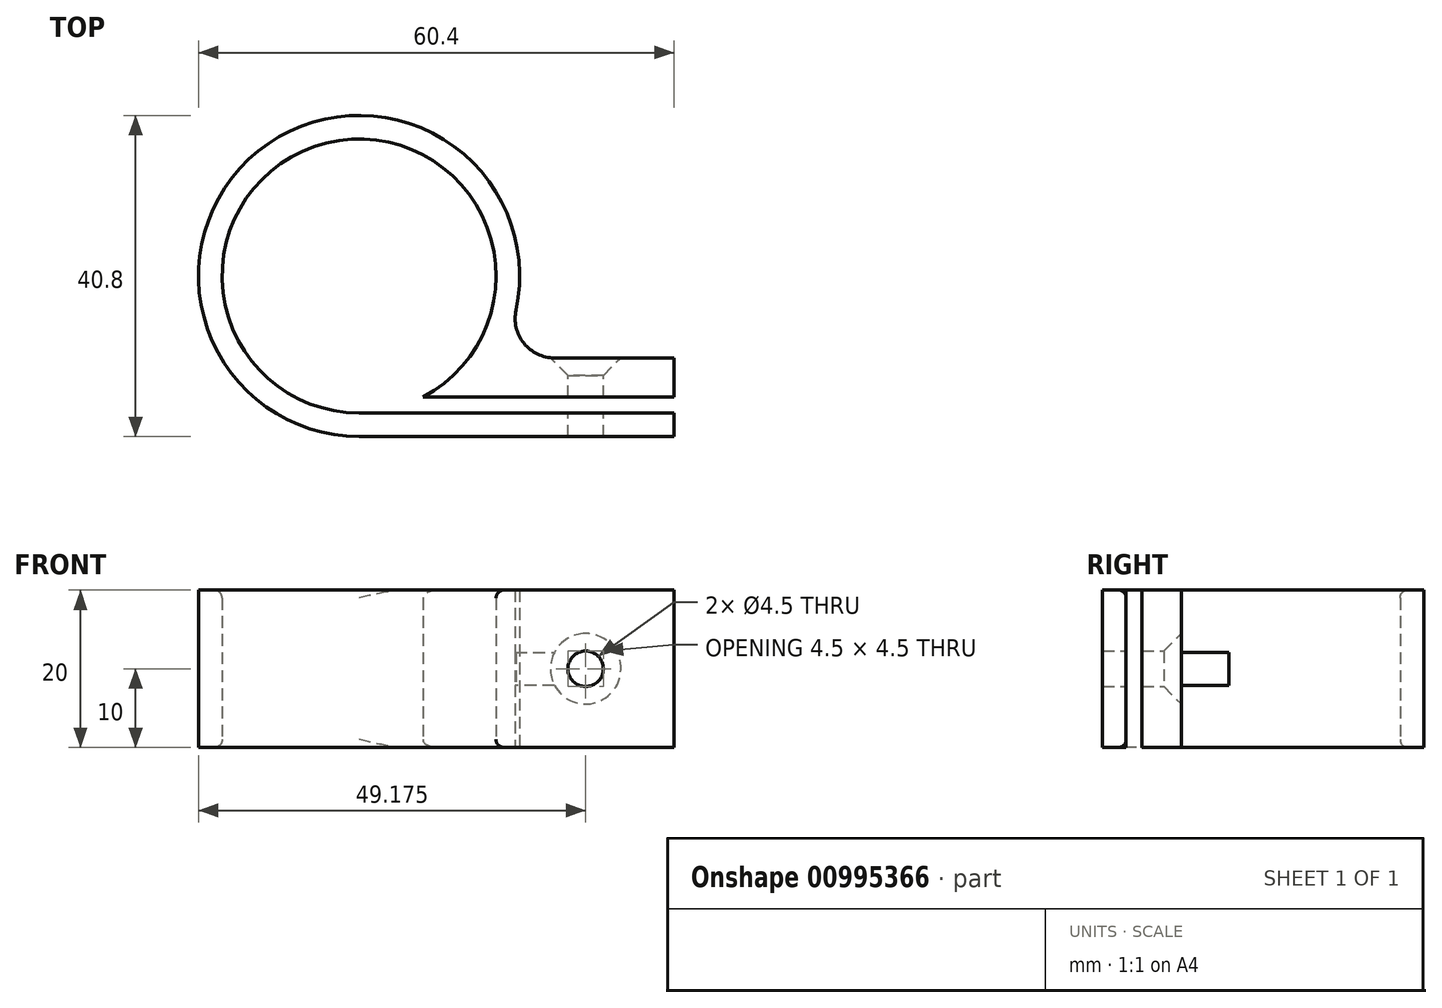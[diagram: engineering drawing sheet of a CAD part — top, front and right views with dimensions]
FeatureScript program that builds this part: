
annotation { "Feature Type Name" : "Feature", "Feature Type Description" : "" }
export const myFeature = defineFeature(function(context is Context, id is Id, definition is map)
    precondition{}
    {
        {
            var Q0;
            Q0=qCreatedBy(makeId("Top.planeOp"),FACE);
            var sketch = newSketch(context, id + "F0", { "sketchPlane" : qUnion([Q0])});
            skCircle(sketch, "E0", {"center": v(0, 0) * mm, "radius": 17.4 * mm});
            skCircle(sketch, "E1.0", {"center": v(0, 0) * mm, "radius": 20.4 * mm});
            skLineSegment(sketch, "E2", {"start": v(0, -20.4) * mm, "end": v(40, -20.4) * mm});
            skLineSegment(sketch, "E3", {"start": v(40, -20.4) * mm, "end": v(40, -10.4) * mm});
            skLineSegment(sketch, "E4", {"start": v(40, -10.4) * mm, "end": v(17.55, -10.4) * mm});
            skLineSegment(sketch, "E5", {"start": v(40, -15.4) * mm, "end": v(8.1, -15.4) * mm});
            skLineSegment(sketch, "E6", {"start": v(40, -17.4) * mm, "end": v(-5.83, -17.4) * mm});
            skSolve(sketch);
        }
        {
            var Q0;
            {var subQ3=sQuery(id+"F0.wireOp",EDGE,"E5");var subQ7=sQuery(id+"F0.wireOp",EDGE,"E0");var subQ8=makeQuery(id+"F0.imprint","INTERSECT",VERTEX,{"derivedFrom":[subQ7,subQ3]});Q0=makeQuery(id+"F0.imprint","IMPRINT",FACE,{"disambiguationData":[TD([[makeQuery(id+"F0.imprint","IMPRINT",EDGE,{"disambiguationData":[TD([[subQ8,-1.0]])],"derivedFrom":subQ7}),-1.0]])]});}
            var Q1;
            {var subQ0=sQuery(id+"F0.wireOp",EDGE,"E2");Q1=makeQuery(id+"F0.imprint","IMPRINT",FACE,{"disambiguationData":[TD([[makeQuery(id+"F0.imprint","IMPRINT",EDGE,{"derivedFrom":subQ0}),1.0]])]});}
            var Q2;
            {var subQ0=sQuery(id+"F0.wireOp",EDGE,"E4");Q2=makeQuery(id+"F0.imprint","IMPRINT",FACE,{"disambiguationData":[TD([[makeQuery(id+"F0.imprint","IMPRINT",EDGE,{"derivedFrom":subQ0}),1.0]])]});}
            extrude(context, id + "F1", {"entities" : qUnion([Q0, Q1, Q2]), "depth" : 20 * mm, "offsetDistance" : 25 * mm});
        }
        {
            var Q0;
            Q0=makeQuery(id+"F1.opExtrude","SWEPT_FACE",FACE,{"disambiguationData":[OSD([sQuery(id+"F0.wireOp",EDGE,"E4")])]});
            var sketch = newSketch(context, id + "F2", { "sketchPlane" : qUnion([Q0])});
            skLineSegment(sketch, "E7.0.0", {"start": v(-40, 0) * mm, "end": v(-17.55, 0) * mm});
            skLineSegment(sketch, "E7.0.1", {"start": v(-17.55, 0) * mm, "end": v(-17.55, 20) * mm});
            skLineSegment(sketch, "E7.0.2", {"start": v(-17.55, 20) * mm, "end": v(-40, 20) * mm});
            skLineSegment(sketch, "E7.0.3", {"start": v(-40, 20) * mm, "end": v(-40, 0) * mm});
            skLineSegment(sketch, "E8", {"start": v(-40, 20) * mm, "end": v(-17.55, 0) * mm, "construction": true});
            skLineSegment(sketch, "E9", {"start": v(-17.55, 20) * mm, "end": v(-40, 0) * mm, "construction": true});
            skPoint(sketch, "E10", {"position": v(-28.77, 10) * mm});
            skSolve(sketch);
        }
        {
            var Q0;
            Q0=sQuery(id+"F2.wireOp",VERTEX,"E10");
            var Q1;
            Q1=makeQuery(id+"F1.opExtrude","SWEPT_BODY",BODY,{"disambiguationData":[OSD([sQuery(id+"F0.wireOp",EDGE,"E0"),sQuery(id+"F0.wireOp",EDGE,"E1.0"),sQuery(id+"F0.wireOp",EDGE,"E2"),sQuery(id+"F0.wireOp",EDGE,"E3"),sQuery(id+"F0.wireOp",EDGE,"E4"),sQuery(id+"F0.wireOp",EDGE,"E5"),sQuery(id+"F0.wireOp",EDGE,"E6")])]});
            hole(context, id + "F3", {"style" : HoleStyle.C_SINK, "endStyle" : HoleEndStyle.THROUGH, "standardTappedOrClearance" : lookupTablePath({ "fit" : "Normal", "standard" : "ISO", "size" : "M4", "type" : "Clearance" }), "standardBlindInLast" : lookupTablePath({ "fit" : "Normal", "standard" : "ISO", "engagement" : "75%", "pitch" : "0.7 mm", "size" : "M4", "type" : "Clearance & tapped" }), "holeDiameter" : 4.5 * mm, "cSinkDiameter" : 8.96 * mm, "cSinkAngle" : 90 * degree, "majorDiameter" : 5 * mm, "tappedDepth" : 12 * mm, "tapClearance" : 3, "locations" : qUnion([Q0]), "scope" : qUnion([Q1])});
        }
        {
            var Q0;
            Q0=makeQuery(id+"F1.opExtrude","SWEPT_EDGE",EDGE,{"disambiguationData":[OSD([sQuery(id+"F0.wireOp",EDGE,"E1.0"),sQuery(id+"F0.wireOp",EDGE,"E4")])]});
            fillet(context, id + "F4", {"entities" : qUnion([Q0]), "radius" : 5 * mm, "tangentPropagation" : true, "allowEdgeOverflow" : false});
        }
        {
            var Q0;
            Q0=makeQuery(id+"F1.opExtrude","CAP_EDGE",EDGE,{"disambiguationData":[OSD([sQuery(id+"F0.wireOp",EDGE,"E0")])],"isStart":true});
            var Q1;
            Q1=makeQuery(id+"F1.opExtrude","CAP_EDGE",EDGE,{"disambiguationData":[OSD([sQuery(id+"F0.wireOp",EDGE,"E0")])],"isStart":false});
            fillet(context, id + "F5", {"entities" : qUnion([Q0, Q1]), "radius" : 1 * mm, "allowEdgeOverflow" : false});
        }
    });
